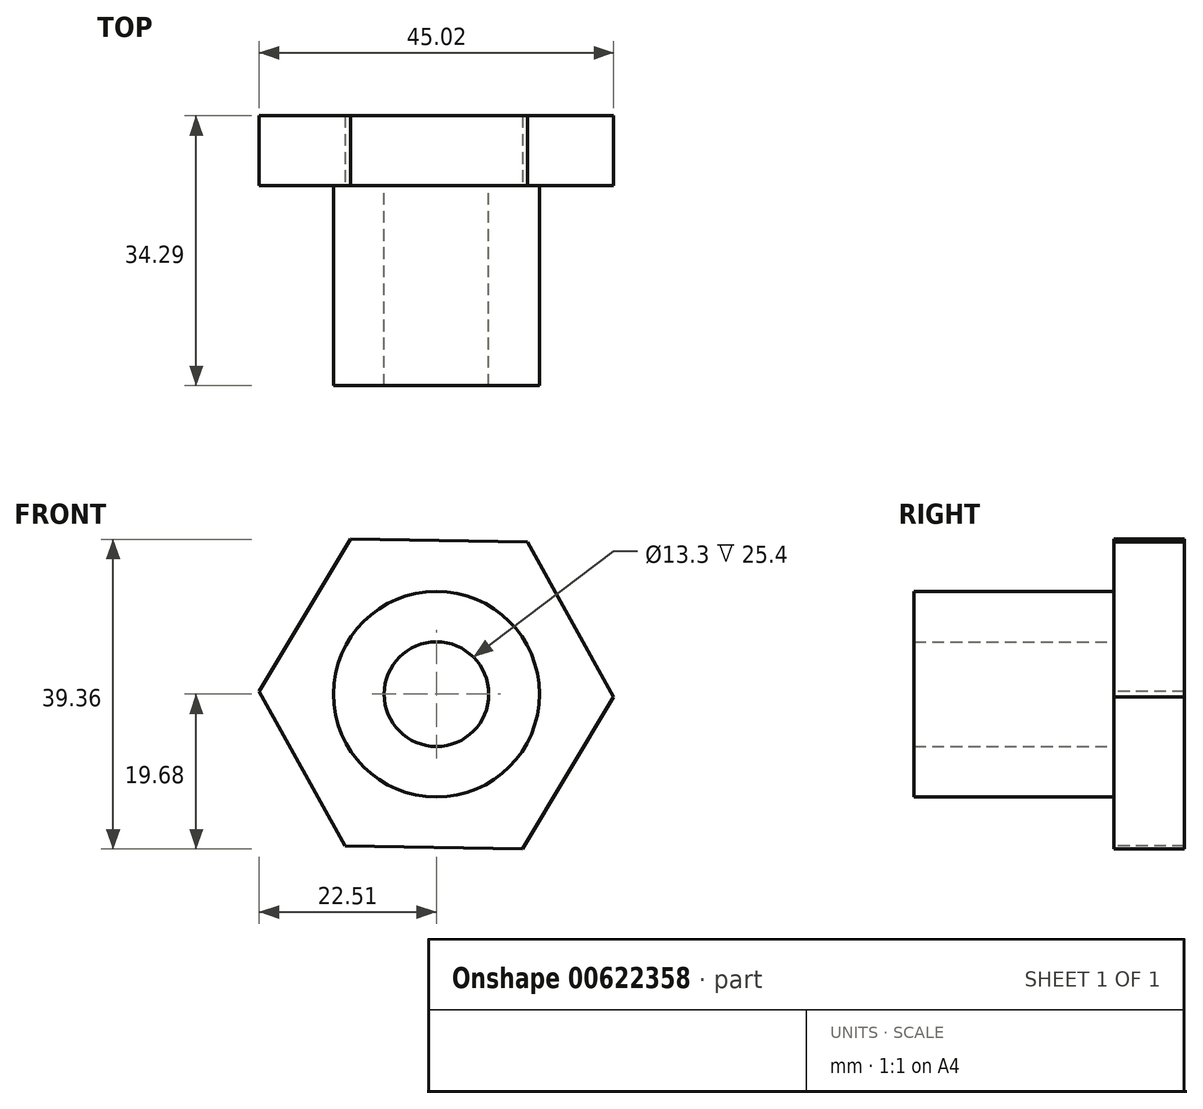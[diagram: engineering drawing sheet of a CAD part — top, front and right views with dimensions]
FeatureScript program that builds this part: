
annotation { "Feature Type Name" : "Feature", "Feature Type Description" : "" }
export const myFeature = defineFeature(function(context is Context, id is Id, definition is map)
    precondition{}
    {
        {
            var Q0;
            Q0=qCreatedBy(makeId("Front.planeOp"),FACE);
            var sketch = newSketch(context, id + "F0", { "sketchPlane" : qUnion([Q0])});
            skCircle(sketch, "E0", {"center": v(0, 0) * mm, "radius": 13.08 * mm});
            skCircle(sketch, "E1", {"center": v(0, 0) * mm, "radius": 6.65 * mm});
            skSolve(sketch);
        }
        {
            var Q0;
            Q0=makeQuery(id+"F0.imprint","IMPRINT",FACE,{"disambiguationData":[TD([[makeQuery(id+"F0.imprint","IMPRINT",EDGE,{"derivedFrom":sQuery(id+"F0.wireOp",EDGE,"E0")}),1.0]])]});
            extrude(context, id + "F1", {"entities" : qUnion([Q0]), "depth" : 25.4 * mm, "offsetDistance" : 25.4 * mm});
        }
        {
            var Q0;
            Q0=qCreatedBy(makeId("Front.planeOp"),FACE);
            var sketch = newSketch(context, id + "F2", { "sketchPlane" : qUnion([Q0])});
            skCircle(sketch, "E2.cCircle", {"center": v(0, 0) * mm, "radius": 19.5 * mm, "construction": true});
            skLineSegment(sketch, "E2.0", {"start": v(-22.5, 0.38) * mm, "end": v(-10.93, 19.68) * mm});
            skLineSegment(sketch, "E2.1", {"start": v(-10.93, 19.68) * mm, "end": v(11.58, 19.3) * mm});
            skLineSegment(sketch, "E2.2", {"start": v(11.58, 19.3) * mm, "end": v(22.5, -0.38) * mm});
            skLineSegment(sketch, "E2.3", {"start": v(22.5, -0.38) * mm, "end": v(10.93, -19.68) * mm});
            skLineSegment(sketch, "E2.4", {"start": v(10.93, -19.68) * mm, "end": v(-11.58, -19.3) * mm});
            skLineSegment(sketch, "E2.5", {"start": v(-11.58, -19.3) * mm, "end": v(-22.5, 0.38) * mm});
            skPoint(sketch, "E2.0.midPoint", {"position": v(-16.72, 10.03) * mm});
            skSolve(sketch);
        }
        {
            var Q0;
            Q0 = qSketchRegion(id + "F2", true);
            extrude(context, id + "F3", {"entities" : qUnion([Q0]), "operationType" : NewBodyOperationType.ADD, "oppositeDirection" : true, "depth" : 8.9 * mm, "offsetDistance" : 25.4 * mm});
        }
    });
